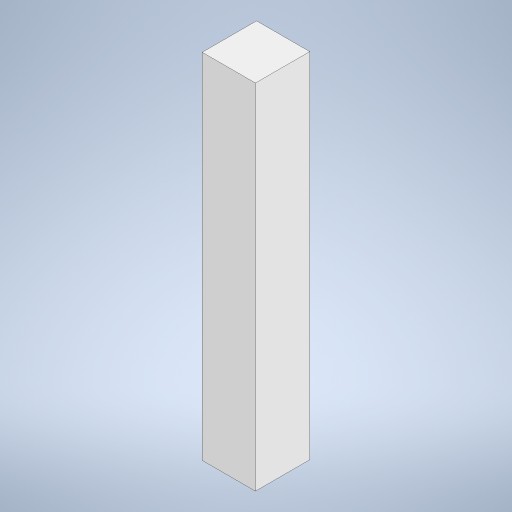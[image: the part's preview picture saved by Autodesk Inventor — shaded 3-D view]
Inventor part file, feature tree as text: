
AUTODESK INVENTOR PART (.ipt)
format: ipt  version: 2024 (Build 280153000, 153)  size: 224,768 bytes
history: native  units: in
note: dims shown in document units (in); Inventor stores cm internally (conversion verified against a paired STEP export)
features: extrude x1, sketch x1
ambient origin geometry x8: Origin, YZ Plane, XZ Plane, XY Plane, X Axis, Y Axis, Z Axis, Center Point
bodies: Solid1 (feature_tree)
feature tree (2):
  extrude  "Extrusion1"  Depth=11.75in
  sketch  "Sketch1"  dims[d2=12.0in d3=11.75in d4=78.0in d5=0.0in]
